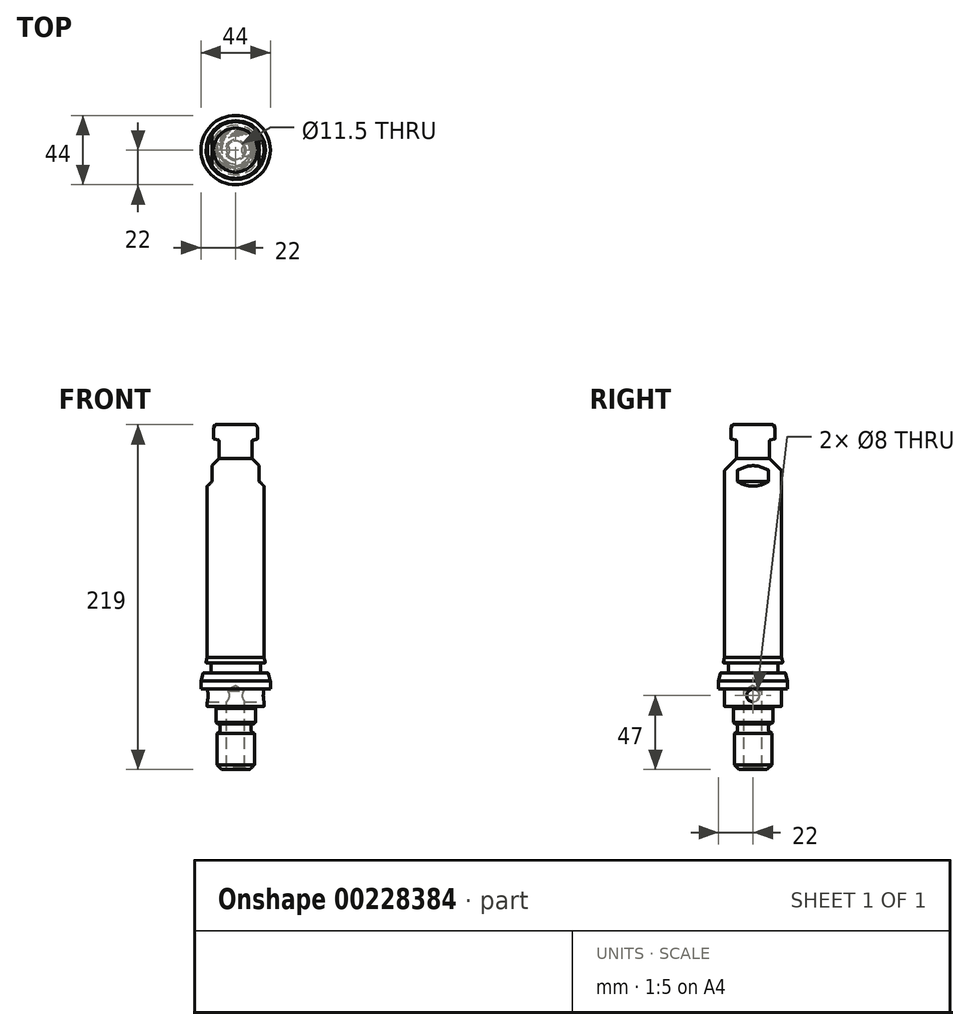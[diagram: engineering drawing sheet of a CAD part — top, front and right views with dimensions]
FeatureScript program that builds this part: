
annotation { "Feature Type Name" : "Feature", "Feature Type Description" : "" }
export const myFeature = defineFeature(function(context is Context, id is Id, definition is map)
    precondition{}
    {
        {
            var Q0;
            Q0=qCreatedBy(makeId("Front.planeOp"),FACE);
            var sketch = newSketch(context, id + "F0", { "sketchPlane" : qUnion([Q0])});
            skLineSegment(sketch, "E0", {"start": v(0, 179) * mm, "end": v(-12.56, 179) * mm});
            skLineSegment(sketch, "E1", {"start": v(-5.75, 10) * mm, "end": v(-5.75, -38.5) * mm});
            skLineSegment(sketch, "E2", {"start": v(-5.75, -38.5) * mm, "end": v(-6.62, -40) * mm});
            skLineSegment(sketch, "E3", {"start": v(-6.62, -40) * mm, "end": v(-8.95, -40) * mm});
            skLineSegment(sketch, "E4", {"start": v(-8.95, -40) * mm, "end": v(-11.95, -37) * mm});
            skLineSegment(sketch, "E5", {"start": v(-11.95, -37) * mm, "end": v(-11.95, -17) * mm});
            skLineSegment(sketch, "E6", {"start": v(-11.95, -17) * mm, "end": v(-10.55, -16.2) * mm});
            skArc(sketch, "E7", {"start": v(-10.55, -16.2) * mm, "mid": v(-10, -15.64) * mm, "end": v(-9.8, -14.9) * mm});
            skLineSegment(sketch, "E8", {"start": v(-9.8, -14.9) * mm, "end": v(-9.8, -12.5) * mm});
            skArc(sketch, "E9", {"start": v(-9.8, -12.5) * mm, "mid": v(-10.24, -11.44) * mm, "end": v(-11.3, -11) * mm});
            skLineSegment(sketch, "E10", {"start": v(-11.3, -11) * mm, "end": v(-11.5, -11) * mm});
            skLineSegment(sketch, "E11", {"start": v(-11.5, -11) * mm, "end": v(-12.5, -10) * mm});
            skLineSegment(sketch, "E12", {"start": v(-12.5, -10) * mm, "end": v(-12.5, -1.2) * mm});
            skLineSegment(sketch, "E13", {"start": v(-12.5, -1.2) * mm, "end": v(-12.35, -0.95) * mm});
            skArc(sketch, "E14", {"start": v(-12.35, -0.95) * mm, "mid": v(-12.31, -0.85) * mm, "end": v(-12.3, -0.75) * mm});
            skLineSegment(sketch, "E15", {"start": v(-12.3, -0.75) * mm, "end": v(-12.3, -0.2) * mm});
            skArc(sketch, "E16", {"start": v(-12.3, -0.2) * mm, "mid": v(-12.42, 0.08) * mm, "end": v(-12.7, 0.2) * mm});
            skLineSegment(sketch, "E17", {"start": v(-12.7, 0.2) * mm, "end": v(-13.13, 0.2) * mm});
            skArc(sketch, "E18", {"start": v(-13.13, 0.2) * mm, "mid": v(-13.2, 0.2) * mm, "end": v(-13.27, 0.18) * mm});
            skLineSegment(sketch, "E19", {"start": v(-13.27, 0.18) * mm, "end": v(-13.75, 0) * mm});
            skLineSegment(sketch, "E20", {"start": v(-13.75, 0) * mm, "end": v(-17.9, 0) * mm});
            skArc(sketch, "E21", {"start": v(-18, 0.3) * mm, "mid": v(-17.97, 0.14) * mm, "end": v(-17.9, 0) * mm});
            skLineSegment(sketch, "E22", {"start": v(-18, 0.3) * mm, "end": v(-18, 11.28) * mm});
            skArc(sketch, "E23", {"start": v(-17.85, 150.15) * mm, "mid": v(-17.96, 149.98) * mm, "end": v(-18, 149.8) * mm});
            skLineSegment(sketch, "E24", {"start": v(-17.85, 150.15) * mm, "end": v(-10.5, 157.5) * mm});
            skLineSegment(sketch, "E25", {"start": v(-10.5, 157.5) * mm, "end": v(-10.5, 168.68) * mm});
            skArc(sketch, "E26", {"start": v(-10.5, 168.68) * mm, "mid": v(-10.6, 168.98) * mm, "end": v(-10.87, 169.16) * mm});
            skLineSegment(sketch, "E27", {"start": v(-10.87, 169.16) * mm, "end": v(-13.63, 169.9) * mm});
            skArc(sketch, "E28", {"start": v(-14, 170.38) * mm, "mid": v(-13.9, 170.08) * mm, "end": v(-13.63, 169.9) * mm});
            skLineSegment(sketch, "E29", {"start": v(-14, 170.38) * mm, "end": v(-14, 176.87) * mm});
            skArc(sketch, "E30", {"start": v(-13.93, 177.12) * mm, "mid": v(-13.98, 177) * mm, "end": v(-14, 176.87) * mm});
            skLineSegment(sketch, "E31", {"start": v(-13.93, 177.12) * mm, "end": v(-12.99, 178.75) * mm});
            skArc(sketch, "E32", {"start": v(-12.56, 179) * mm, "mid": v(-12.8, 178.93) * mm, "end": v(-12.99, 178.75) * mm});
            skLineSegment(sketch, "E33", {"start": v(0, 16.21) * mm, "end": v(0, -16.21) * mm, "construction": true});
            skLineSegment(sketch, "E34", {"start": v(-5.75, 10) * mm, "end": v(0, 13.32) * mm});
            skLineSegment(sketch, "E35", {"start": v(0, 13.32) * mm, "end": v(0, 179) * mm});
            skLineSegment(sketch, "E36", {"start": v(-30.19, 28.25) * mm, "end": v(-19, 28.25) * mm, "construction": true});
            skLineSegment(sketch, "E37", {"start": v(-19, 28.25) * mm, "end": v(-19, 38.58) * mm, "construction": true});
            skLineSegment(sketch, "E38", {"start": v(-19, 28.25) * mm, "end": v(-20.59, 22.32) * mm, "construction": true});
            skLineSegment(sketch, "E39", {"start": v(-22, 16.28) * mm, "end": v(-20.71, 21.1) * mm});
            skLineSegment(sketch, "E40", {"start": v(-22, 16.28) * mm, "end": v(-22, 11.28) * mm});
            skLineSegment(sketch, "E41", {"start": v(-22, 11.28) * mm, "end": v(-18, 11.28) * mm});
            skLineSegment(sketch, "E42.trimOffspring", {"start": v(-18, 31.2) * mm, "end": v(-18, 149.8) * mm});
            skLineSegment(sketch, "E43", {"start": v(-20, 32.07) * mm, "end": v(-20, 24.52) * mm, "construction": true});
            skLineSegment(sketch, "E44", {"start": v(-20, 24.52) * mm, "end": v(-12.71, 24.52) * mm, "construction": true});
            skLineSegment(sketch, "E45", {"start": v(-18.6, 27.76) * mm, "end": v(-16.3, 27.76) * mm});
            skLineSegment(sketch, "E46", {"start": v(-15.7, 27.16) * mm, "end": v(-15.7, 21.88) * mm});
            skLineSegment(sketch, "E47", {"start": v(-16.3, 21.28) * mm, "end": v(-20.47, 21.28) * mm});
            skPoint(sketch, "E48", {"position": v(-15.7, 24.52) * mm});
            skLineSegment(sketch, "E49.trimOffspring", {"start": v(-18.84, 28.07) * mm, "end": v(-18, 31.2) * mm});
            skPoint(sketch, "E50.visualSharp", {"position": v(-15.7, 27.76) * mm});
            skArc(sketch, "E50.filletArc", {"start": v(-15.7, 27.16) * mm, "mid": v(-15.88, 27.58) * mm, "end": v(-16.3, 27.76) * mm});
            skPoint(sketch, "E51.visualSharp", {"position": v(-15.7, 21.28) * mm});
            skArc(sketch, "E51.filletArc", {"start": v(-16.3, 21.28) * mm, "mid": v(-15.88, 21.45) * mm, "end": v(-15.7, 21.88) * mm});
            skPoint(sketch, "E52.visualSharp", {"position": v(-18.92, 27.76) * mm});
            skArc(sketch, "E52.filletArc", {"start": v(-18.84, 28.07) * mm, "mid": v(-18.8, 27.86) * mm, "end": v(-18.6, 27.76) * mm});
            skPoint(sketch, "E53.visualSharp", {"position": v(-20.66, 21.28) * mm});
            skArc(sketch, "E53.filletArc", {"start": v(-20.47, 21.28) * mm, "mid": v(-20.62, 21.23) * mm, "end": v(-20.71, 21.1) * mm});
            skSolve(sketch);
        }
        {
            var Q0;
            Q0 = qSketchRegion(id + "F0", true);
            var Q1;
            Q1=sQuery(id+"F0.wireOp",EDGE,"E33");
            revolve(context, id + "F1", {"entities" : qUnion([Q0]), "axis" : qUnion([Q1]), "revolveType" : RevolveType.FULL});
        }
        {
            var Q0;
            Q0=qCreatedBy(makeId("Front.planeOp"),FACE);
            var sketch = newSketch(context, id + "F2", { "sketchPlane" : qUnion([Q0])});
            skLineSegment(sketch, "E54.bottom", {"start": v(15, 155) * mm, "end": v(20, 155) * mm});
            skLineSegment(sketch, "E54.left", {"start": v(15, 155) * mm, "end": v(15, 143) * mm});
            skLineSegment(sketch, "E55", {"start": v(15, 143) * mm, "end": v(20, 138) * mm});
            skLineSegment(sketch, "E56", {"start": v(20, 138) * mm, "end": v(20, 155) * mm});
            skSolve(sketch);
        }
        {
            var Q0;
            Q0 = qSketchRegion(id + "F2", true);
            extrude(context, id + "F3", {"entities" : qUnion([Q0]), "depth" : 12 * mm, "hasSecondDirection" : true, "secondDirectionOppositeDirection" : true, "secondDirectionDepth" : 12 * mm});
        }
        {
            var Q0;
            Q0=makeQuery(id+"F3.opExtrude","SWEPT_BODY",BODY,{"disambiguationData":[OSD([sQuery(id+"F2.wireOp",EDGE,"E54.bottom"),sQuery(id+"F2.wireOp",EDGE,"E54.top"),sQuery(id+"F2.wireOp",EDGE,"E54.left"),sQuery(id+"F2.wireOp",EDGE,"E54.right")])]});
            var Q1;
            Q1=makeQuery(id+"F1.opRevolve","SWEPT_FACE",FACE,{"disambiguationData":[OSD([sQuery(id+"F0.wireOp",EDGE,"E42.trimOffspring")])]});
            circularPattern(context, id + "F4", {"entities" : qUnion([Q0]), "axis" : qUnion([Q1]), "angle" : 360 * degree, "instanceCount" : 2, "equalSpace" : true});
        }
        {
            var Q0;
            Q0=makeQuery(id+"F4.opPattern","COPY",BODY,{"derivedFrom":makeQuery(id+"F3.opExtrude","SWEPT_BODY",BODY,{"disambiguationData":[OSD([sQuery(id+"F2.wireOp",EDGE,"E54.bottom"),sQuery(id+"F2.wireOp",EDGE,"E54.top"),sQuery(id+"F2.wireOp",EDGE,"E54.left"),sQuery(id+"F2.wireOp",EDGE,"E54.right")])]}),"instanceName":"1"});
            var Q1;
            Q1=makeQuery(id+"F3.opExtrude","SWEPT_BODY",BODY,{"disambiguationData":[OSD([sQuery(id+"F2.wireOp",EDGE,"E54.bottom"),sQuery(id+"F2.wireOp",EDGE,"E54.top"),sQuery(id+"F2.wireOp",EDGE,"E54.left"),sQuery(id+"F2.wireOp",EDGE,"E54.right")])]});
            var Q2;
            Q2=makeQuery(id+"F1.opRevolve","SWEPT_BODY",BODY,{"disambiguationData":[OSD([sQuery(id+"F0.wireOp",EDGE,"E0"),sQuery(id+"F0.wireOp",EDGE,"E1"),sQuery(id+"F0.wireOp",EDGE,"E2"),sQuery(id+"F0.wireOp",EDGE,"E3"),sQuery(id+"F0.wireOp",EDGE,"E4"),sQuery(id+"F0.wireOp",EDGE,"E5"),sQuery(id+"F0.wireOp",EDGE,"E6"),sQuery(id+"F0.wireOp",EDGE,"E7"),sQuery(id+"F0.wireOp",EDGE,"E8"),sQuery(id+"F0.wireOp",EDGE,"E9"),sQuery(id+"F0.wireOp",EDGE,"E10"),sQuery(id+"F0.wireOp",EDGE,"E11"),sQuery(id+"F0.wireOp",EDGE,"E12"),sQuery(id+"F0.wireOp",EDGE,"E13"),sQuery(id+"F0.wireOp",EDGE,"E14"),sQuery(id+"F0.wireOp",EDGE,"E15"),sQuery(id+"F0.wireOp",EDGE,"E16"),sQuery(id+"F0.wireOp",EDGE,"E17"),sQuery(id+"F0.wireOp",EDGE,"E18"),sQuery(id+"F0.wireOp",EDGE,"E19"),sQuery(id+"F0.wireOp",EDGE,"E20"),sQuery(id+"F0.wireOp",EDGE,"E21"),sQuery(id+"F0.wireOp",EDGE,"E22"),sQuery(id+"F0.wireOp",EDGE,"E23"),sQuery(id+"F0.wireOp",EDGE,"E24"),sQuery(id+"F0.wireOp",EDGE,"E25"),sQuery(id+"F0.wireOp",EDGE,"E26"),sQuery(id+"F0.wireOp",EDGE,"E27"),sQuery(id+"F0.wireOp",EDGE,"E28"),sQuery(id+"F0.wireOp",EDGE,"E29"),sQuery(id+"F0.wireOp",EDGE,"E30"),sQuery(id+"F0.wireOp",EDGE,"E31"),sQuery(id+"F0.wireOp",EDGE,"E32"),sQuery(id+"F0.wireOp",EDGE,"E34"),sQuery(id+"F0.wireOp",EDGE,"E35"),sQuery(id+"F0.wireOp",EDGE,"E39"),sQuery(id+"F0.wireOp",EDGE,"E40"),sQuery(id+"F0.wireOp",EDGE,"E41"),sQuery(id+"F0.wireOp",EDGE,"E42.trimOffspring")])]});
            booleanBodies(context, id + "F5", {"operationType" : BooleanOperationType.SUBTRACTION, "tools" : qUnion([Q0, Q1]), "targets" : qUnion([Q2])});
        }
        {
            var Q0;
            Q0=qCreatedBy(makeId("Right.planeOp"),FACE);
            var sketch = newSketch(context, id + "F6", { "sketchPlane" : qUnion([Q0])});
            skCircle(sketch, "E57", {"center": v(0, 7) * mm, "radius": 4 * mm});
            skSolve(sketch);
        }
        {
            var Q0;
            Q0 = qSketchRegion(id + "F6", true);
            extrude(context, id + "F7", {"entities" : qUnion([Q0]), "operationType" : NewBodyOperationType.REMOVE, "endBound" : BoundingType.THROUGH_ALL, "oppositeDirection" : true, "depth" : 25 * mm, "hasSecondDirection" : true, "secondDirectionBound" : SecondDirectionBoundingType.THROUGH_ALL, "secondDirectionOppositeDirection" : false, "secondDirectionDepth" : 25 * mm});
        }
    });
